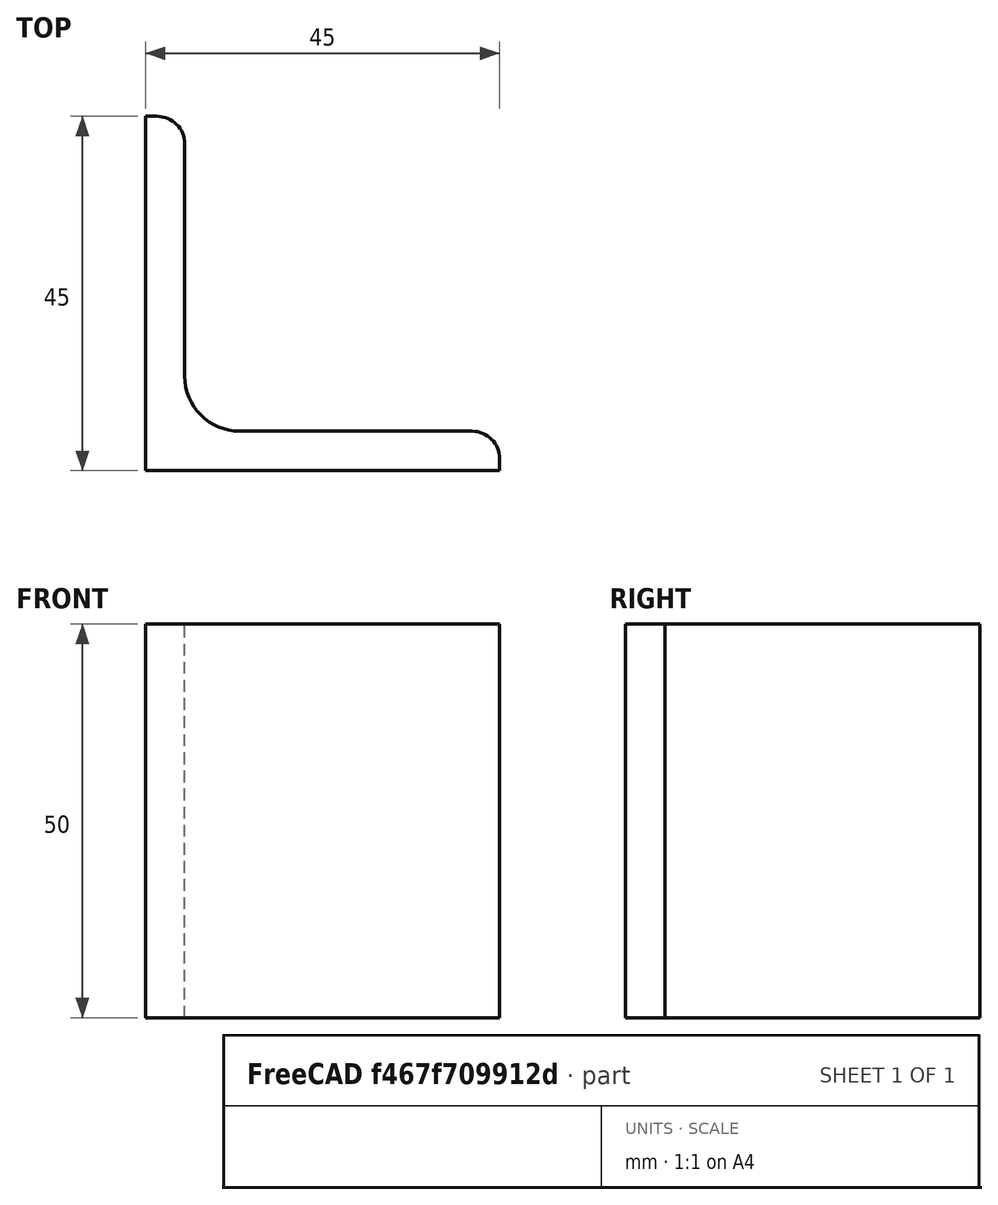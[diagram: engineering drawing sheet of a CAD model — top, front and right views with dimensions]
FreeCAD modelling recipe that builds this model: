
FCSTD DOCUMENT  (FreeCAD 0.15R4671 (Git))
Label: Angle Bar L45x45x5 EN10056 S235JR
License: All rights reserved
LicenseURL: http://en.wikipedia.org/wiki/All_rights_reserved
objects: Sketcher::SketchObject×1, Part::Extrusion×1
note: 2 computed .brp shape members not serialized (recipe doc carries the construction recipe); baked Part::Feature solids carry a one-line shape summary decoded from their .brp

FEATURE [Sketcher::SketchObject] Sketch
  sketch-geometry (9):
    g0: LineSegment StartX=0 StartY=0 StartZ=0 EndX=45 EndY=0 EndZ=0
    g1: LineSegment StartX=45 StartY=0 StartZ=0 EndX=45 EndY=1.5 EndZ=0
    g2: LineSegment StartX=41.5 StartY=5 StartZ=0 EndX=12 EndY=5 EndZ=0
    g3: LineSegment StartX=0 StartY=0 StartZ=0 EndX=0 EndY=45 EndZ=0
    g4: LineSegment StartX=0 StartY=45 StartZ=0 EndX=1.5 EndY=45 EndZ=0
    g5: LineSegment StartX=5 StartY=41.5 StartZ=0 EndX=5 EndY=12 EndZ=0
    g6: ArcOfCircle CenterX=12 CenterY=12 CenterZ=0 NormalX=0 NormalY=0 NormalZ=1 Radius=7 StartAngle=3.14159 EndAngle=4.71239
    g7: ArcOfCircle CenterX=1.5 CenterY=41.5 CenterZ=0 NormalX=0 NormalY=0 NormalZ=1 Radius=3.5 StartAngle=0 EndAngle=1.5708
    g8: ArcOfCircle CenterX=41.5 CenterY=1.5 CenterZ=0 NormalX=0 NormalY=0 NormalZ=1 Radius=3.5 StartAngle=0 EndAngle=1.5708
  constraints (23):
    c: Coincident(g0,g-1)
    c: Horizontal(g0)
    c: Coincident(g1,g0)
    c: Vertical(g1)
    c: Horizontal(g2)
    c: Coincident(g3,g-1)
    c: Vertical(g3)
    c: Coincident(g4,g3)
    c: Horizontal(g4)
    c: Vertical(g5)
    c: Tangent(g5,g6) = -1.5708
    c: Tangent(g2,g6) = 1.5708
    c: Tangent(g4,g7) = 1.5708
    c: Tangent(g5,g7) = 1.5708
    c: Tangent(g2,g8) = -1.5708
    c: Tangent(g1,g8) = -1.5708
    c: DistanceX(g0) = 45
    c: DistanceY(g3) = 45
    c: DistanceY(g0,g2) = 5
    c: DistanceX(g3,g5) = 5
    c: Radius(g6) = 7
    c: Radius(g8) = 3.5
    c: Radius(g7) = 3.5
FEATURE [Part::Extrusion] Extrude  label="Angle Bar L45x45x5 EN10056 S235JR"
  Base = -> Sketch
  Dir = (0,0,50)
  Solid = true
